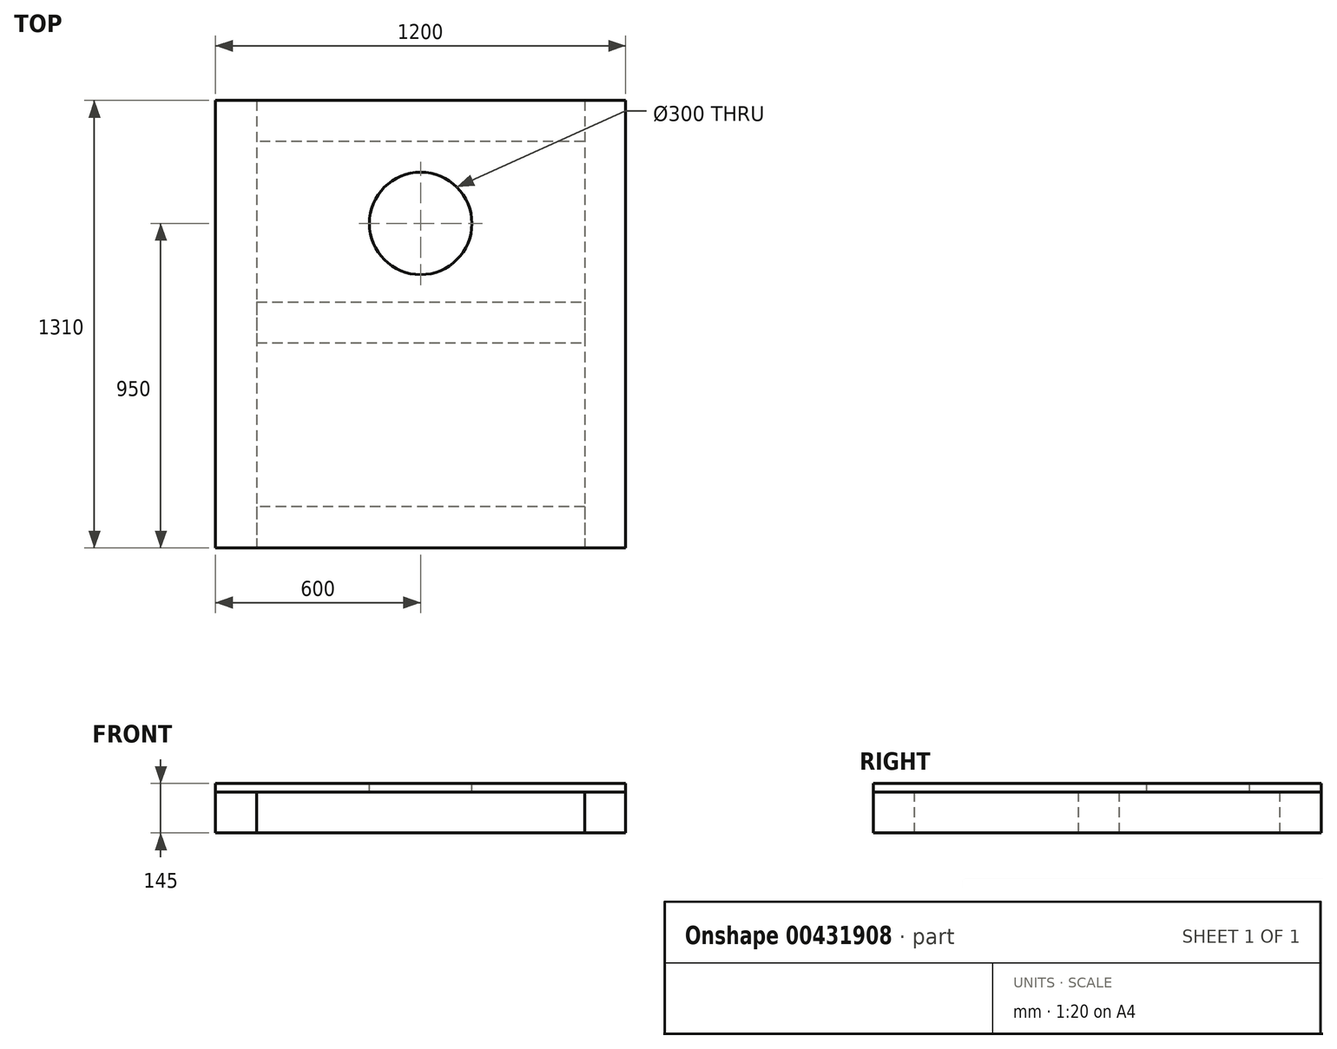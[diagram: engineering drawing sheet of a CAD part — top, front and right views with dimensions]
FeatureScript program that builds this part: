
annotation { "Feature Type Name" : "Feature", "Feature Type Description" : "" }
export const myFeature = defineFeature(function(context is Context, id is Id, definition is map)
    precondition{}
    {
        {
            var Q0;
            Q0=qCreatedBy(makeId("Top.planeOp"),FACE);
            var sketch = newSketch(context, id + "F0", { "sketchPlane" : qUnion([Q0])});
            skLineSegment(sketch, "E0.bottom", {"start": v(-600, 0) * mm, "end": v(600, 0) * mm});
            skLineSegment(sketch, "E0.top", {"start": v(-600, 1310) * mm, "end": v(600, 1310) * mm});
            skLineSegment(sketch, "E0.left", {"start": v(-600, 1310) * mm, "end": v(-600, 0) * mm});
            skLineSegment(sketch, "E0.right", {"start": v(600, 1310) * mm, "end": v(600, 0) * mm});
            skCircle(sketch, "E1", {"center": v(0, 950) * mm, "radius": 150 * mm});
            skSolve(sketch);
        }
        {
            var Q0;
            Q0 = qSketchRegion(id + "F0", true);
            extrude(context, id + "F1", {"entities" : qUnion([Q0]), "oppositeDirection" : true, "depth" : 25 * mm, "offsetDistance" : 25 * mm});
        }
        {
            var Q0;
            Q0=qCreatedBy(makeId("Top.planeOp"),FACE);
            cPlane(context, id + "F2", {"entities" : qUnion([Q0]), "cplaneType" : CPlaneType.OFFSET, "offset" : 25 * mm, "oppositeDirection" : true, "width" : 150 * mm, "height" : 150 * mm});
        }
        {
            var Q0;
            Q0=qCreatedBy(id+"F2.planeOp",FACE);
            var sketch = newSketch(context, id + "F3", { "sketchPlane" : qUnion([Q0])});
            skLineSegment(sketch, "E2.bottom", {"start": v(-600, 0) * mm, "end": v(600, 0) * mm, "construction": true});
            skLineSegment(sketch, "E2.top", {"start": v(-600, 1310) * mm, "end": v(600, 1310) * mm, "construction": true});
            skLineSegment(sketch, "E2.left", {"start": v(-600, 1310) * mm, "end": v(-600, 120) * mm, "construction": true});
            skLineSegment(sketch, "E2.right", {"start": v(600, 1310) * mm, "end": v(600, 0) * mm, "construction": true});
            skLineSegment(sketch, "E3.bottom", {"start": v(600, 1310) * mm, "end": v(-600, 1310) * mm});
            skLineSegment(sketch, "E3.top", {"start": v(480, 1190) * mm, "end": v(-480, 1190) * mm});
            skLineSegment(sketch, "E3.left", {"start": v(600, 1310) * mm, "end": v(600, 1190) * mm});
            skLineSegment(sketch, "E3.right", {"start": v(-600, 1310) * mm, "end": v(-600, 1190) * mm});
            skLineSegment(sketch, "E4.bottom", {"start": v(600, 0) * mm, "end": v(-600, 0) * mm});
            skLineSegment(sketch, "E4.top", {"start": v(480, 120) * mm, "end": v(-480, 120) * mm});
            skLineSegment(sketch, "E4.left", {"start": v(600, 0) * mm, "end": v(600, 120) * mm});
            skLineSegment(sketch, "E4.right", {"start": v(-600, 0) * mm, "end": v(-600, 120) * mm});
            skLineSegment(sketch, "E5.left", {"start": v(600, 1190) * mm, "end": v(600, 120) * mm});
            skLineSegment(sketch, "E5.right", {"start": v(480, 1310) * mm, "end": v(480, 0) * mm});
            skLineSegment(sketch, "E6.left", {"start": v(-600, 1190) * mm, "end": v(-600, 120) * mm});
            skLineSegment(sketch, "E6.right", {"start": v(-480, 1310) * mm, "end": v(-480, 0) * mm});
            skLineSegment(sketch, "E7.bottom", {"start": v(-480, 720) * mm, "end": v(480, 720) * mm});
            skLineSegment(sketch, "E7.top", {"start": v(-480, 600) * mm, "end": v(480, 600) * mm});
            skLineSegment(sketch, "E7.left", {"start": v(-480, 720) * mm, "end": v(-480, 600) * mm});
            skLineSegment(sketch, "E7.right", {"start": v(480, 720) * mm, "end": v(480, 600) * mm});
            skSolve(sketch);
        }
        {
            var Q0;
            Q0=makeQuery(id+"F3.imprint","IMPRINT",FACE,{"disambiguationData":[TD([[makeQuery(id+"F3.imprint","IMPRINT",EDGE,{"derivedFrom":sQuery(id+"F3.wireOp",EDGE,"E3.bottom")}),1.0]])]});
            var Q1;
            Q1=makeQuery(id+"F3.imprint","IMPRINT",FACE,{"disambiguationData":[TD([[makeQuery(id+"F3.imprint","IMPRINT",EDGE,{"derivedFrom":sQuery(id+"F3.wireOp",EDGE,"E4.bottom")}),-1.0]])]});
            extrude(context, id + "F4", {"entities" : qUnion([Q0, Q1]), "oppositeDirection" : true, "depth" : 120 * mm, "offsetDistance" : 25 * mm});
        }
        {
            var Q0;
            {var subQ6=sQuery(id+"F3.wireOp",EDGE,"E3.right");Q0=makeQuery(id+"F3.imprint","IMPRINT",FACE,{"disambiguationData":[TD([[makeQuery(id+"F3.imprint","IMPRINT",EDGE,{"derivedFrom":subQ6}),1.0]])]});}
            var Q1;
            {var subQ4=sQuery(id+"F3.wireOp",EDGE,"E3.left");Q1=makeQuery(id+"F3.imprint","IMPRINT",FACE,{"disambiguationData":[TD([[makeQuery(id+"F3.imprint","IMPRINT",EDGE,{"derivedFrom":subQ4}),-1.0]])]});}
            extrude(context, id + "F5", {"entities" : qUnion([Q0, Q1]), "oppositeDirection" : true, "depth" : 120 * mm, "offsetDistance" : 25 * mm});
        }
        {
            var Q0;
            Q0=makeQuery(id+"F3.imprint","IMPRINT",FACE,{"disambiguationData":[TD([[makeQuery(id+"F3.imprint","IMPRINT",EDGE,{"derivedFrom":sQuery(id+"F3.wireOp",EDGE,"E7.bottom")}),-1.0]])]});
            extrude(context, id + "F6", {"entities" : qUnion([Q0]), "oppositeDirection" : true, "depth" : 120 * mm, "offsetDistance" : 25 * mm});
        }
    });
